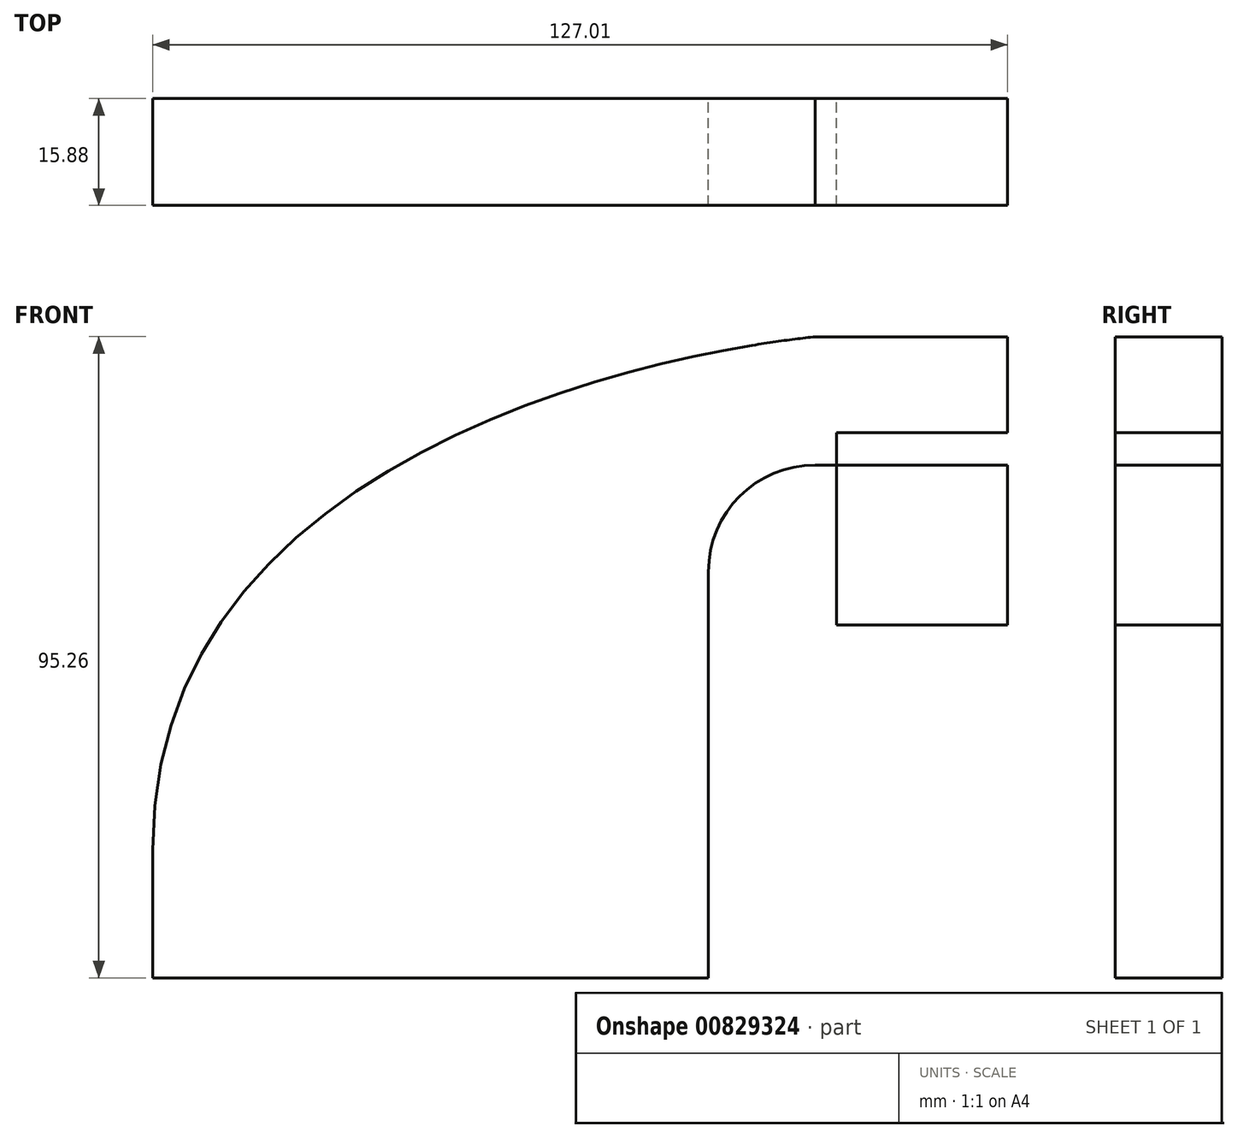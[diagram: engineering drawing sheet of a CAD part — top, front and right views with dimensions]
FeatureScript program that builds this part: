
annotation { "Feature Type Name" : "Feature", "Feature Type Description" : "" }
export const myFeature = defineFeature(function(context is Context, id is Id, definition is map)
    precondition{}
    {
        {
            var Q0;
            Q0=qCreatedBy(makeId("Front.planeOp"),FACE);
            var sketch = newSketch(context, id + "F0", { "sketchPlane" : qUnion([Q0])});
            skLineSegment(sketch, "E0.bottom", {"start": v(-41.28, -9.53) * mm, "end": v(41.28, -9.53) * mm});
            skLineSegment(sketch, "E0.top", {"start": v(-41.28, 9.53) * mm, "end": v(41.28, 9.53) * mm});
            skLineSegment(sketch, "E0.left", {"start": v(-41.28, -9.53) * mm, "end": v(-41.28, 9.53) * mm});
            skLineSegment(sketch, "E0.right", {"start": v(41.28, -9.53) * mm, "end": v(41.28, 9.53) * mm});
            skPoint(sketch, "E0.middle", {"position": v(0, 0) * mm});
            skLineSegment(sketch, "E1.bottom", {"start": v(60.32, 42.88) * mm, "end": v(111.12, 42.88) * mm});
            skLineSegment(sketch, "E1.top", {"start": v(60.32, 71.45) * mm, "end": v(111.12, 71.45) * mm});
            skLineSegment(sketch, "E1.left", {"start": v(60.32, 42.88) * mm, "end": v(60.32, 71.45) * mm});
            skLineSegment(sketch, "E1.right", {"start": v(111.12, 42.88) * mm, "end": v(111.12, 71.45) * mm});
            skPoint(sketch, "E1.middle", {"position": v(85.72, 57.16) * mm});
            skLineSegment(sketch, "E2", {"start": v(41.27, 9.53) * mm, "end": v(41.27, 50.8) * mm});
            skArc(sketch, "E3", {"start": v(41.27, 50.8) * mm, "mid": v(45.92, 62.03) * mm, "end": v(57.15, 66.68) * mm});
            skLineSegment(sketch, "E4", {"start": v(57.15, 66.68) * mm, "end": v(85.72, 66.68) * mm});
            skPoint(sketch, "E4.endSnap0", {"position": v(85.72, 42.88) * mm});
            skLineSegment(sketch, "E5.0", {"start": v(57.15, 85.72) * mm, "end": v(85.72, 85.72) * mm});
            skArc(sketch, "E5.1", {"start": v(22.23, 50.8) * mm, "mid": v(32.45, 75.5) * mm, "end": v(57.15, 85.73) * mm});
            skLineSegment(sketch, "E5.2", {"start": v(22.23, 9.53) * mm, "end": v(22.23, 50.8) * mm});
            skLineSegment(sketch, "E6", {"start": v(85.73, 42.88) * mm, "end": v(85.72, 85.72) * mm});
            skFitSpline(sketch, "E7", {"points": [v(-41.28, 9.53) * mm, v(57.15, 85.73) * mm], "startDerivative": vector(-0.5, 171.13) * mm, "endDerivative": vector(83.7, 8.85) * mm});
            skSolve(sketch);
        }
        {
            var Q0;
            Q0=makeQuery(id+"F0.imprint","IMPRINT",FACE,{"disambiguationData":[TD([[makeQuery(id+"F0.imprint","IMPRINT",EDGE,{"derivedFrom":sQuery(id+"F0.wireOp",EDGE,"E0.bottom")}),1.0]])]});
            var Q1;
            {var subQ12=sQuery(id+"F0.wireOp",EDGE,"E2");Q1=makeQuery(id+"F0.imprint","IMPRINT",FACE,{"disambiguationData":[TD([[makeQuery(id+"F0.imprint","IMPRINT",EDGE,{"derivedFrom":subQ12}),1.0]])]});}
            var Q2;
            {var subQ0=sQuery(id+"F0.wireOp",EDGE,"E1.left");var subQ1=sQuery(id+"F0.wireOp",EDGE,"E1.bottom");var subQ2=makeQuery(id+"F0.imprint","INTERSECT",VERTEX,{"derivedFrom":[subQ1,subQ0]});Q2=makeQuery(id+"F0.imprint","IMPRINT",FACE,{"disambiguationData":[TD([[makeQuery(id+"F0.imprint","IMPRINT",EDGE,{"disambiguationData":[TD([[subQ2,-1.0]])],"derivedFrom":subQ1}),1.0]])]});}
            var Q3;
            {var subQ3=sQuery(id+"F0.wireOp",EDGE,"E5.2");Q3=makeQuery(id+"F0.imprint","IMPRINT",FACE,{"disambiguationData":[TD([[makeQuery(id+"F0.imprint","IMPRINT",EDGE,{"derivedFrom":subQ3}),1.0]])]});}
            extrude(context, id + "F1", {"entities" : qUnion([Q0, Q1, Q2, Q3]), "endBound" : BoundingType.SYMMETRIC, "depth" : 15.88 * mm, "offsetDistance" : 25.4 * mm});
        }
    });
